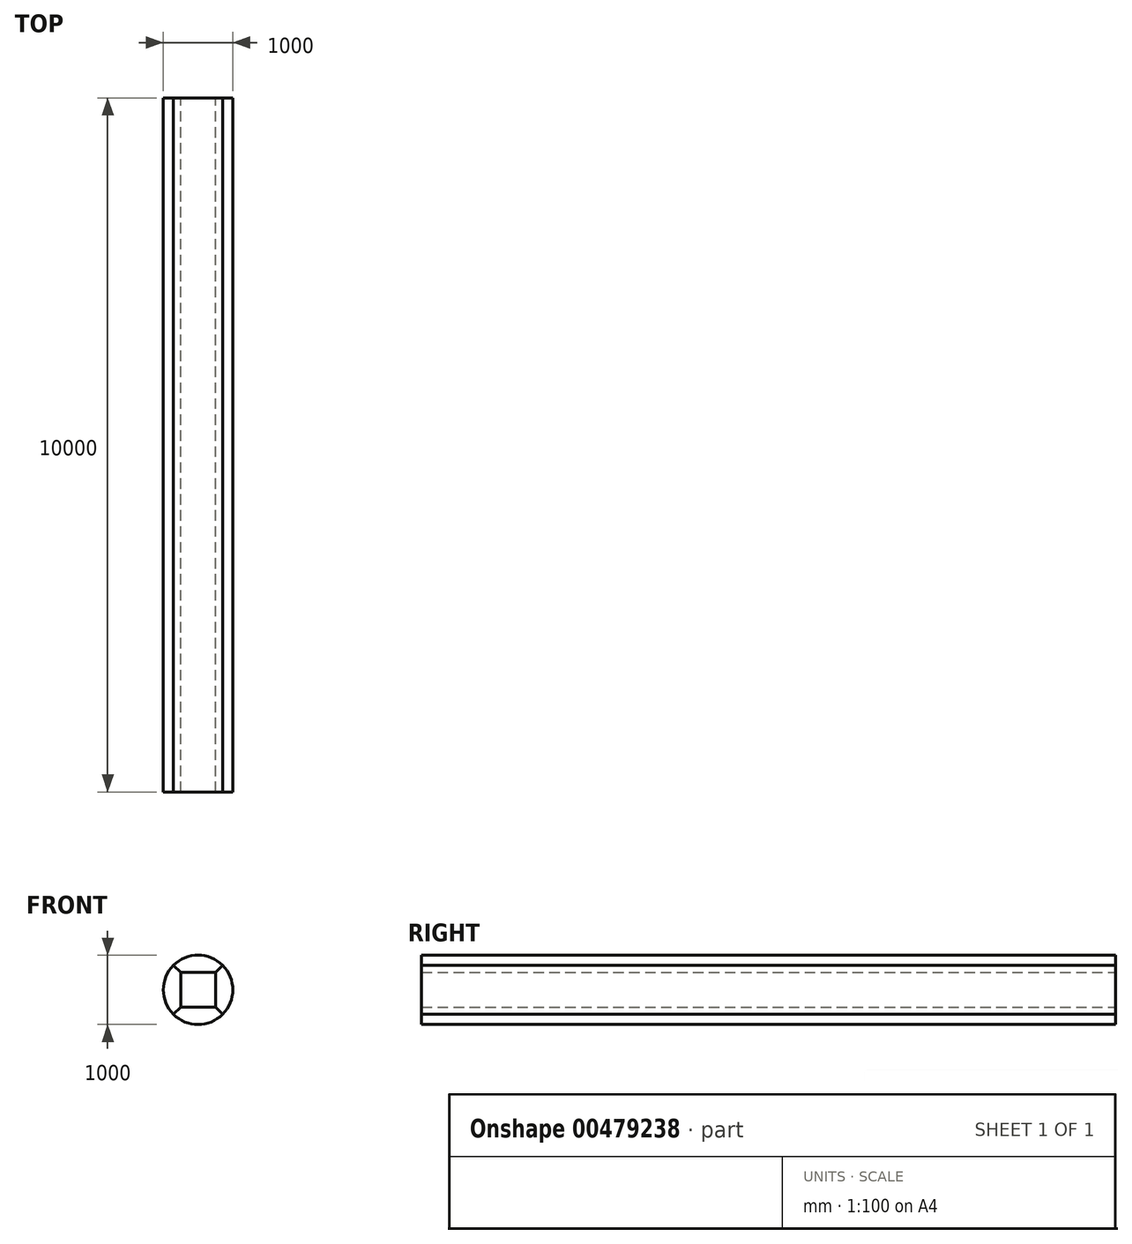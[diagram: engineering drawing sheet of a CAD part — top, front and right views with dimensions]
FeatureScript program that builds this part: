
annotation { "Feature Type Name" : "Feature", "Feature Type Description" : "" }
export const myFeature = defineFeature(function(context is Context, id is Id, definition is map)
    precondition{}
    {
        {
            var Q0;
            Q0=qCreatedBy(makeId("Front.planeOp"),FACE);
            var sketch = newSketch(context, id + "F0", { "sketchPlane" : qUnion([Q0])});
            skLineSegment(sketch, "E0", {"start": v(-250, 250) * mm, "end": v(250, 250) * mm});
            skArc(sketch, "E1", {"start": v(353.55, 353.55) * mm, "mid": v(0, 500) * mm, "end": v(-353.55, 353.55) * mm});
            skLineSegment(sketch, "E2", {"start": v(-250, 250) * mm, "end": v(-353.55, 353.55) * mm});
            skLineSegment(sketch, "E3", {"start": v(250, 250) * mm, "end": v(353.55, 353.55) * mm});
            skLineSegment(sketch, "E4", {"start": v(0, 0) * mm, "end": v(0, 500) * mm, "construction": true});
            skSolve(sketch);
        }
        {
            var Q0;
            Q0 = qSketchRegion(id + "F0", true);
            extrude(context, id + "F1", {"entities" : qUnion([Q0]), "depth" : 10000 * mm});
        }
        {
            var Q0;
            Q0=qCreatedBy(makeId("Right.planeOp"),FACE);
            var sketch = newSketch(context, id + "F2", { "sketchPlane" : qUnion([Q0])});
            skLineSegment(sketch, "E5", {"start": v(0, 0) * mm, "end": v(-1000, 0) * mm, "construction": true});
            skSolve(sketch);
        }
        {
            var Q0;
            Q0=makeQuery(id+"F1.opExtrude","SWEPT_BODY",BODY,{"disambiguationData":[OSD([sQuery(id+"F0.wireOp",EDGE,"E0"),sQuery(id+"F0.wireOp",EDGE,"E1"),sQuery(id+"F0.wireOp",EDGE,"E2"),sQuery(id+"F0.wireOp",EDGE,"E3")])]});
            var Q1;
            Q1=sQuery(id+"F2.wireOp",EDGE,"E5");
            circularPattern(context, id + "F3", {"entities" : qUnion([Q0]), "axis" : qUnion([Q1]), "angle" : 360 * degree, "instanceCount" : 4, "equalSpace" : true});
        }
        {
            var Q0;
            Q0=qCreatedBy(makeId("Front.planeOp"),FACE);
            var sketch = newSketch(context, id + "F4", { "sketchPlane" : qUnion([Q0])});
            skLineSegment(sketch, "E6.bottom", {"start": v(250, -250) * mm, "end": v(-250, -250) * mm});
            skLineSegment(sketch, "E6.top", {"start": v(250, 250) * mm, "end": v(-250, 250) * mm});
            skLineSegment(sketch, "E6.left", {"start": v(250, -250) * mm, "end": v(250, 250) * mm});
            skLineSegment(sketch, "E6.right", {"start": v(-250, -250) * mm, "end": v(-250, 250) * mm});
            skSolve(sketch);
        }
        {
            var Q0;
            Q0 = qSketchRegion(id + "F4", true);
            extrude(context, id + "F5", {"entities" : qUnion([Q0]), "depth" : 10000 * mm});
        }
    });
